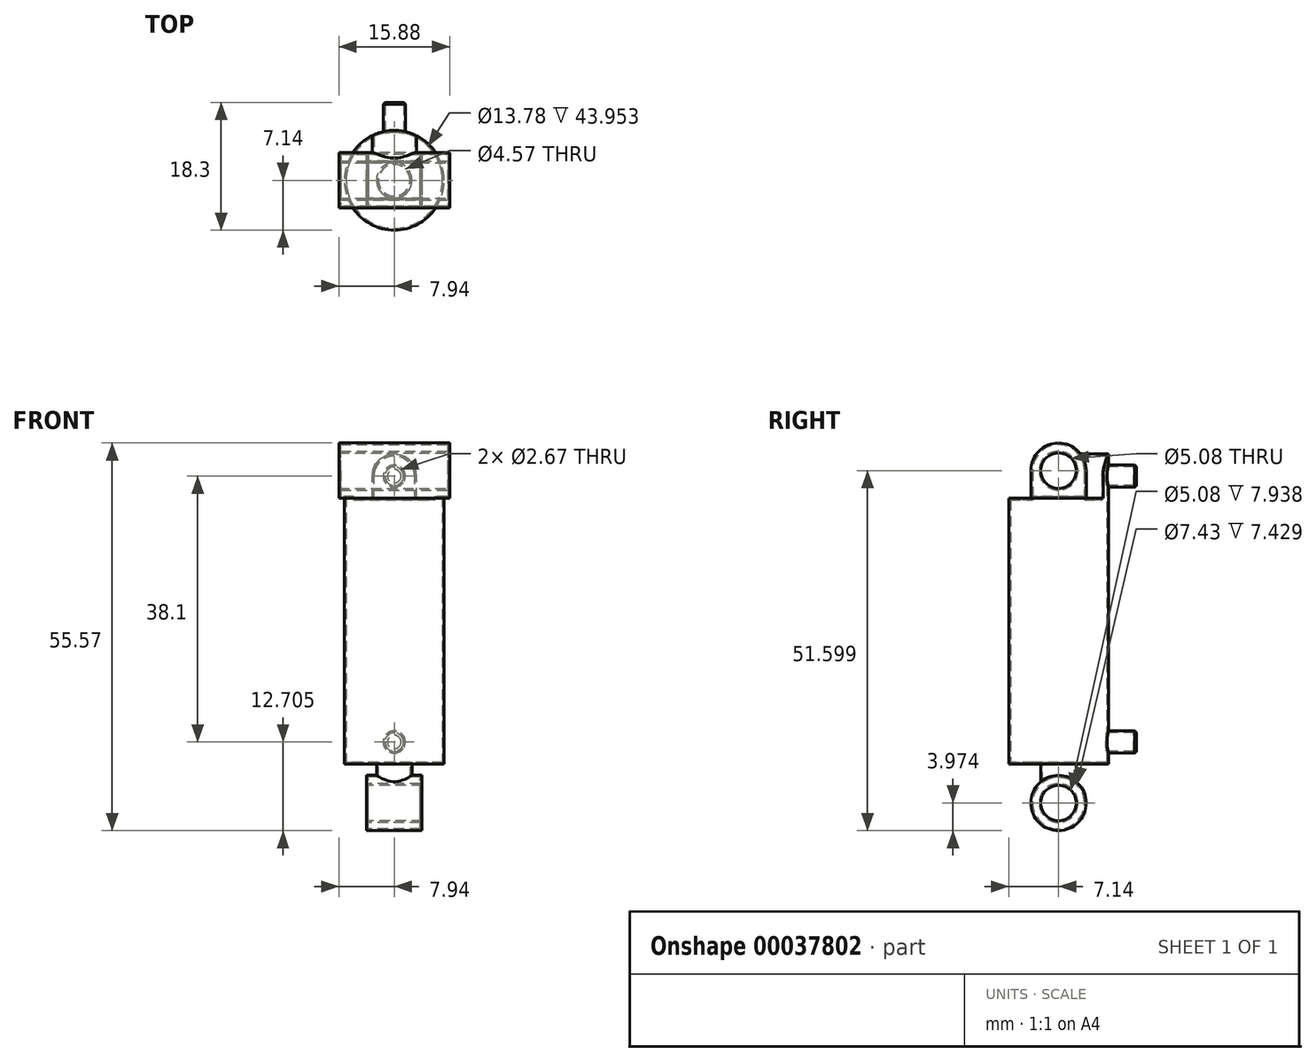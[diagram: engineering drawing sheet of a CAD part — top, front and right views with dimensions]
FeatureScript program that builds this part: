
annotation { "Feature Type Name" : "Feature", "Feature Type Description" : "" }
export const myFeature = defineFeature(function(context is Context, id is Id, definition is map)
    precondition{}
    {
        {
            var Q0;
            Q0=qCreatedBy(makeId("Top.planeOp"),FACE);
            var sketch = newSketch(context, id + "F0", { "sketchPlane" : qUnion([Q0])});
            skCircle(sketch, "E0", {"center": v(0, 0) * mm, "radius": 7.14 * mm});
            skSolve(sketch);
        }
        {
            var Q0;
            Q0=qSketchRegion(id+"F0",true);
            extrude(context, id + "F1", {"entities" : qUnion([Q0]), "depth" : 38.1 * mm});
        }
        {
            var Q0;
            Q0=makeQuery(id+"F1.opExtrude","CAP_FACE",FACE,{"disambiguationData":[OSD([sQuery(id+"F0.wireOp",EDGE,"E0")])],"isStart":false});
            var sketch = newSketch(context, id + "F2", { "sketchPlane" : qUnion([Q0])});
            skLineSegment(sketch, "E1.rect.bottom", {"start": v(7.94, 3.97) * mm, "end": v(-7.94, 3.97) * mm});
            skLineSegment(sketch, "E1.rect.top", {"start": v(7.94, -3.97) * mm, "end": v(-7.94, -3.97) * mm});
            skLineSegment(sketch, "E1.rect.left", {"start": v(7.94, 3.97) * mm, "end": v(7.94, -3.97) * mm});
            skLineSegment(sketch, "E1.rect.right", {"start": v(-7.94, 3.97) * mm, "end": v(-7.94, -3.97) * mm});
            skPoint(sketch, "E1.rect.middle", {"position": v(0, 0) * mm});
            skSolve(sketch);
        }
        {
            var Q0;
            Q0=qSketchRegion(id+"F2",true);
            extrude(context, id + "F3", {"entities" : qUnion([Q0]), "operationType" : NewBodyOperationType.ADD, "depth" : 7.94 * mm});
        }
        {
            var Q0;
            Q0=makeQuery(id+"F3.opExtrude","CAP_EDGE",EDGE,{"disambiguationData":[OSD([sQuery(id+"F2.wireOp",EDGE,"E1.rect.bottom")])],"isStart":false});
            var Q1;
            Q1=makeQuery(id+"F3.opExtrude","CAP_EDGE",EDGE,{"disambiguationData":[OSD([sQuery(id+"F2.wireOp",EDGE,"E1.rect.top")])],"isStart":false});
            fillet(context, id + "F4", {"entities" : qUnion([Q0, Q1]), "radius" : 3.97 * mm, "tangentPropagation" : true, "allowEdgeOverflow" : false});
        }
        {
            var Q0;
            Q0=makeQuery(id+"F3.opExtrude","SWEPT_FACE",FACE,{"disambiguationData":[OSD([sQuery(id+"F2.wireOp",EDGE,"E1.rect.left")])]});
            var sketch = newSketch(context, id + "F5", { "sketchPlane" : qUnion([Q0])});
            skCircle(sketch, "E2", {"center": v(0, 42.07) * mm, "radius": 2.54 * mm});
            skSolve(sketch);
        }
        {
            var Q0;
            Q0=qSketchRegion(id+"F5",true);
            var Q1;
            Q1=makeQuery(id+"F3.opExtrude","SWEPT_FACE",FACE,{"disambiguationData":[OSD([sQuery(id+"F2.wireOp",EDGE,"E1.rect.right")])]});
            extrude(context, id + "F6", {"entities" : qUnion([Q0]), "operationType" : NewBodyOperationType.REMOVE, "endBound" : BoundingType.UP_TO_SURFACE, "oppositeDirection" : true, "endBoundEntityFace" : qUnion([Q1]), "depth" : 25.4 * mm});
        }
        {
            var Q0;
            Q0=makeQuery(id+"F3.opExtrude","SWEPT_FACE",FACE,{"disambiguationData":[OSD([sQuery(id+"F2.wireOp",EDGE,"E1.rect.bottom")])]});
            var sketch = newSketch(context, id + "F7", { "sketchPlane" : qUnion([Q0])});
            skLineSegment(sketch, "E3.bottom", {"start": v(-3.18, 38.1) * mm, "end": v(3.18, 38.1) * mm});
            skLineSegment(sketch, "E3.top", {"start": v(-3.18, 41.27) * mm, "end": v(3.17, 41.27) * mm});
            skLineSegment(sketch, "E3.left", {"start": v(-3.18, 38.1) * mm, "end": v(-3.18, 41.27) * mm});
            skLineSegment(sketch, "E3.right", {"start": v(3.17, 38.1) * mm, "end": v(3.17, 41.27) * mm});
            skPoint(sketch, "E4", {"position": v(0, 38.1) * mm});
            skArc(sketch, "E5", {"start": v(3.17, 41.27) * mm, "mid": v(0, 44.45) * mm, "end": v(-3.18, 41.27) * mm});
            skSolve(sketch);
        }
        {
            var Q0;
            Q0=qSketchRegion(id+"F7",true);
            var Q1;
            Q1=makeQuery(id+"F1.opExtrude","SWEPT_FACE",FACE,{"disambiguationData":[OSD([sQuery(id+"F0.wireOp",EDGE,"E0")])]});
            var Q2;
            Q2=makeQuery(id+"F4.opFillet","BLEND_FACE",FACE,{"disambiguationData":[OSD([sQuery(id+"F2.wireOp",EDGE,"E1.rect.bottom")])]});
            extrude(context, id + "F8", {"entities" : qUnion([Q0]), "operationType" : NewBodyOperationType.ADD, "endBound" : BoundingType.UP_TO_SURFACE, "endBoundEntityFace" : qUnion([Q1]), "depth" : 25.4 * mm, "hasSecondDirection" : true, "secondDirectionBound" : SecondDirectionBoundingType.UP_TO_SURFACE, "secondDirectionOppositeDirection" : true, "secondDirectionBoundEntityFace" : qUnion([Q2]), "secondDirectionDepth" : 25.4 * mm});
        }
        {
            var Q0;
            Q0=qCreatedBy(makeId("Front.planeOp"),FACE);
            cPlane(context, id + "F9", {"entities" : qUnion([Q0]), "cplaneType" : CPlaneType.OFFSET, "offset" : 6.4 * mm, "oppositeDirection" : true, "width" : 152.4 * mm, "height" : 152.4 * mm});
        }
        {
            var Q0;
            Q0=qCreatedBy(id+"F9.planeOp",FACE);
            var sketch = newSketch(context, id + "F10", { "sketchPlane" : qUnion([Q0])});
            skCircle(sketch, "E6", {"center": v(0, 41.27) * mm, "radius": 1.59 * mm});
            skLineSegment(sketch, "E7", {"start": v(0, 41.27) * mm, "end": v(0, 3.18) * mm, "construction": true});
            skLineSegment(sketch, "E8", {"start": v(0, 3.18) * mm, "end": v(0, 0) * mm, "construction": true});
            skCircle(sketch, "E9", {"center": v(0, 3.18) * mm, "radius": 1.59 * mm});
            skSolve(sketch);
        }
        {
            var Q0;
            Q0=qSketchRegion(id+"F10",true);
            extrude(context, id + "F11", {"entities" : qUnion([Q0]), "operationType" : NewBodyOperationType.ADD, "oppositeDirection" : true, "depth" : 4.76 * mm});
        }
        {
            var Q0;
            Q0=makeQuery(id+"F1.opExtrude","CAP_FACE",FACE,{"disambiguationData":[OSD([sQuery(id+"F0.wireOp",EDGE,"E0")])],"isStart":true});
            var sketch = newSketch(context, id + "F12", { "sketchPlane" : qUnion([Q0])});
            skCircle(sketch, "E10", {"center": v(0, 0) * mm, "radius": 2.54 * mm});
            skSolve(sketch);
        }
        {
            var Q0;
            Q0=qSketchRegion(id+"F12",true);
            extrude(context, id + "F13", {"entities" : qUnion([Q0]), "operationType" : NewBodyOperationType.ADD, "depth" : 1.59 * mm});
        }
        {
            var Q0;
            Q0=makeQuery(id+"F13.opExtrude","CAP_FACE",FACE,{"disambiguationData":[OSD([sQuery(id+"F12.wireOp",EDGE,"E10")])],"isStart":false});
            var sketch = newSketch(context, id + "F14", { "sketchPlane" : qUnion([Q0])});
            skLineSegment(sketch, "E11.rect.bottom", {"start": v(3.97, 3.97) * mm, "end": v(-3.97, 3.97) * mm});
            skLineSegment(sketch, "E11.rect.top", {"start": v(3.97, -3.97) * mm, "end": v(-3.97, -3.97) * mm});
            skLineSegment(sketch, "E11.rect.left", {"start": v(3.97, 3.97) * mm, "end": v(3.97, -3.97) * mm});
            skLineSegment(sketch, "E11.rect.right", {"start": v(-3.97, 3.97) * mm, "end": v(-3.97, -3.97) * mm});
            skPoint(sketch, "E11.rect.middle", {"position": v(0, 0) * mm});
            skSolve(sketch);
        }
        {
            var Q0;
            Q0=qSketchRegion(id+"F14",true);
            extrude(context, id + "F15", {"entities" : qUnion([Q0]), "operationType" : NewBodyOperationType.ADD, "depth" : 7.94 * mm});
        }
        {
            var Q0;
            Q0=makeQuery(id+"F15.opExtrude","CAP_EDGE",EDGE,{"disambiguationData":[OSD([sQuery(id+"F14.wireOp",EDGE,"E11.rect.top")])],"isStart":true});
            var Q1;
            Q1=makeQuery(id+"F15.opExtrude","CAP_EDGE",EDGE,{"disambiguationData":[OSD([sQuery(id+"F14.wireOp",EDGE,"E11.rect.top")])],"isStart":false});
            var Q2;
            Q2=makeQuery(id+"F15.opExtrude","CAP_EDGE",EDGE,{"disambiguationData":[OSD([sQuery(id+"F14.wireOp",EDGE,"E11.rect.bottom")])],"isStart":false});
            var Q3;
            Q3=makeQuery(id+"F15.opExtrude","CAP_EDGE",EDGE,{"disambiguationData":[OSD([sQuery(id+"F14.wireOp",EDGE,"E11.rect.bottom")])],"isStart":true});
            fillet(context, id + "F16", {"entities" : qUnion([Q0, Q1, Q2, Q3]), "radius" : 3.97 * mm, "tangentPropagation" : true, "allowEdgeOverflow" : false});
        }
        {
            var Q0;
            Q0=makeQuery(id+"F15.opExtrude","SWEPT_FACE",FACE,{"disambiguationData":[OSD([sQuery(id+"F14.wireOp",EDGE,"E11.rect.right")])]});
            var sketch = newSketch(context, id + "F17", { "sketchPlane" : qUnion([Q0])});
            skCircle(sketch, "E12", {"center": v(0, -5.56) * mm, "radius": 2.54 * mm});
            skSolve(sketch);
        }
        {
            var Q0;
            Q0=qSketchRegion(id+"F17",true);
            var Q1;
            Q1=makeQuery(id+"F15.opExtrude","SWEPT_FACE",FACE,{"disambiguationData":[OSD([sQuery(id+"F14.wireOp",EDGE,"E11.rect.left")])]});
            extrude(context, id + "F18", {"entities" : qUnion([Q0]), "operationType" : NewBodyOperationType.REMOVE, "endBound" : BoundingType.UP_TO_SURFACE, "oppositeDirection" : true, "endBoundEntityFace" : qUnion([Q1]), "depth" : 25.4 * mm});
        }
        {
            var Q0;
            Q0=makeQuery(id+"F11.opExtrude","CAP_EDGE",EDGE,{"disambiguationData":[OSD([sQuery(id+"F10.wireOp",EDGE,"E6")])],"isStart":false});
            var Q1;
            Q1=makeQuery(id+"F11.opExtrude","CAP_EDGE",EDGE,{"disambiguationData":[OSD([sQuery(id+"F10.wireOp",EDGE,"E9")])],"isStart":false});
            chamfer(context, id + "F19", {"entities" : qUnion([Q0, Q1]), "width" : 0.25 * mm, "tangentPropagation" : true});
        }
        {
            var Q0;
            Q0=makeQuery(id+"F11.opExtrude","CAP_FACE",FACE,{"disambiguationData":[OSD([sQuery(id+"F10.wireOp",EDGE,"E9")])],"isStart":false});
            var Q1;
            Q1=makeQuery(id+"F11.opExtrude","CAP_FACE",FACE,{"disambiguationData":[OSD([sQuery(id+"F10.wireOp",EDGE,"E6")])],"isStart":false});
            shell(context, id + "F20", {"entities" : qUnion([Q0, Q1]), "thickness" : 0.25 * mm});
        }
    });
